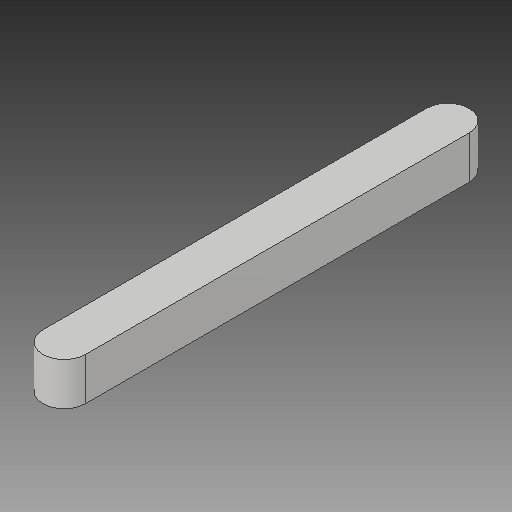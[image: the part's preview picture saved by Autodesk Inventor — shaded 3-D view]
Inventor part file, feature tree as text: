
AUTODESK INVENTOR PART (.ipt)
format: ipt  version: 2017 (Build 210142000, 142)  size: 79,360 bytes
history: native  units: in
note: dims shown in document units (in); Inventor stores cm internally (conversion verified against a paired STEP export)
features: fillet x1
ambient origin geometry x8: Origin, YZ Plane, XZ Plane, XY Plane, X Axis, Y Axis, Z Axis, Center Point
bodies: Solid1 (feature_tree)
feature tree (1):
  fillet  "Fillet1"  [1 undecoded]
note: 1 required parameter value undecoded (feature->parameter linkage not recoverable at this tier; creation-order binding heuristic only, values carry confidence <= 0.55)
